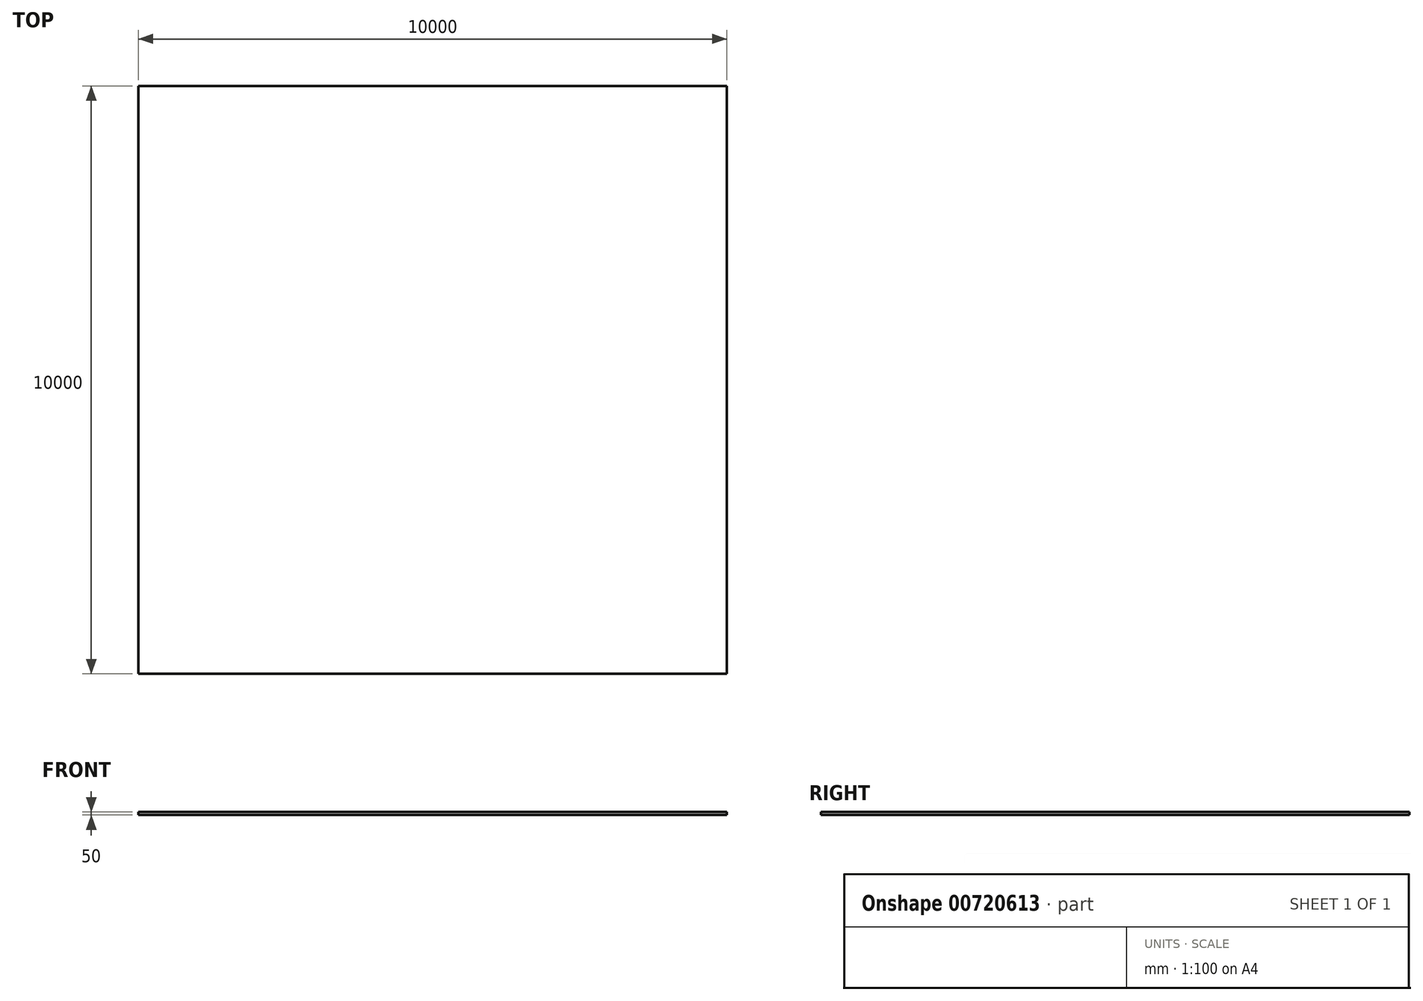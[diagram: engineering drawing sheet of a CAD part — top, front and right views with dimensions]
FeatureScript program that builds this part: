
annotation { "Feature Type Name" : "Feature", "Feature Type Description" : "" }
export const myFeature = defineFeature(function(context is Context, id is Id, definition is map)
    precondition{}
    {
        {
            var Q0;
            Q0=qCreatedBy(makeId("Top.planeOp"),FACE);
            var sketch = newSketch(context, id + "F0", { "sketchPlane" : qUnion([Q0])});
            skLineSegment(sketch, "E0.bottom", {"start": v(-5000, 5000) * mm, "end": v(5000, 5000) * mm});
            skLineSegment(sketch, "E0.top", {"start": v(-5000, -5000) * mm, "end": v(5000, -5000) * mm});
            skLineSegment(sketch, "E0.left", {"start": v(-5000, 5000) * mm, "end": v(-5000, -5000) * mm});
            skLineSegment(sketch, "E0.right", {"start": v(5000, 5000) * mm, "end": v(5000, -5000) * mm});
            skLineSegment(sketch, "E1", {"start": v(-5000, 0) * mm, "end": v(5000, 0) * mm});
            skPoint(sketch, "E1.endSnap0", {"position": v(5000, 0) * mm});
            skLineSegment(sketch, "E2", {"start": v(-2000, 0) * mm, "end": v(-2000, 1000) * mm});
            skSolve(sketch);
        }
        {
            var Q0;
            Q0=makeQuery(id+"F0.imprint","IMPRINT",FACE,{"disambiguationData":[TD([[makeQuery(id+"F0.imprint","IMPRINT",EDGE,{"derivedFrom":sQuery(id+"F0.wireOp",EDGE,"E0.bottom")}),-1.0]])]});
            var Q1;
            {var subQ1=sQuery(id+"F0.wireOp",EDGE,"E0.top");Q1=makeQuery(id+"F0.imprint","IMPRINT",FACE,{"disambiguationData":[TD([[makeQuery(id+"F0.imprint","IMPRINT",EDGE,{"derivedFrom":subQ1}),1.0]])]});}
            extrude(context, id + "F1", {"entities" : qUnion([Q0, Q1]), "oppositeDirection" : true, "depth" : 50 * mm, "offsetDistance" : 25 * mm});
        }
        {
            var Q0;
            Q0=sQuery(id+"F0.wireOp",EDGE,"E2");
            extrude(context, id + "F2", {"bodyType" : ToolBodyType.SURFACE, "surfaceEntities" : qUnion([Q0]), "depth" : 1000 * mm, "offsetDistance" : 25 * mm});
        }
        {
            var Q0;
            {var subQ5=sQuery(id+"F0.wireOp",EDGE,"E0.bottom");Q0=makeQuery(id+"F0.imprint","IMPRINT",FACE,{"disambiguationData":[TD([[makeQuery(id+"F0.imprint","IMPRINT",EDGE,{"derivedFrom":subQ5}),-1.0]])]});}
            var Q1;
            Q1=sQuery(id+"F0.wireOp",EDGE,"E1");
            var Q2;
            Q2=makeQuery(id+"F2.opExtrude","CAP_VERTEX",VERTEX,{"disambiguationData":[OSD([sQuery(id+"F0.wireOp",VERTEX,"E2.start")])],"isStart":false});
            extrude(context, id + "F3", {"entities" : qUnion([Q0]), "bodyType" : ToolBodyType.SURFACE, "surfaceEntities" : qUnion([Q1]), "endBound" : BoundingType.UP_TO_VERTEX, "depth" : 25 * mm, "endBoundEntityVertex" : qUnion([Q2]), "offsetDistance" : 25 * mm});
        }
    });
